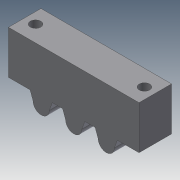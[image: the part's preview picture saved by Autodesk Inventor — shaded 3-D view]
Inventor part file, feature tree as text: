
AUTODESK INVENTOR PART (.ipt)
format: ipt  version: 2014 SP1 (Build 180222100, 222)  size: 58,368 bytes
history: native  units: in
note: dims shown in document units (in); Inventor stores cm internally (conversion verified against a paired STEP export)
features: plane x1
ambient origin geometry x8: Origin, YZ Plane, XZ Plane, XY Plane, X Axis, Y Axis, Z Axis, Center Point
feature tree (1):
  plane  "Work Plane1"
